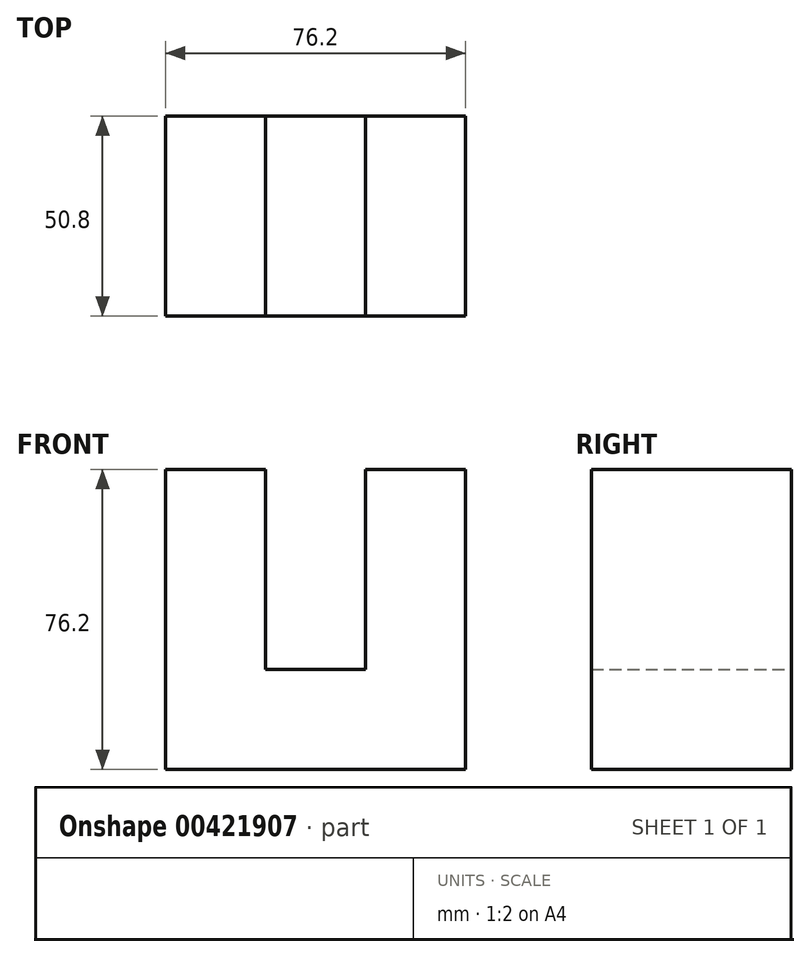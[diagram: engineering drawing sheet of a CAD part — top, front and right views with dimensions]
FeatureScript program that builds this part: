
annotation { "Feature Type Name" : "Feature", "Feature Type Description" : "" }
export const myFeature = defineFeature(function(context is Context, id is Id, definition is map)
    precondition{}
    {
        {
            var Q0;
            Q0=qCreatedBy(makeId("Front.planeOp"),FACE);
            var sketch = newSketch(context, id + "F0", { "sketchPlane" : qUnion([Q0])});
            skLineSegment(sketch, "E0", {"start": v(-51.91, 0) * mm, "end": v(24.29, 0) * mm});
            skLineSegment(sketch, "E1", {"start": v(-51.91, 0) * mm, "end": v(-51.91, 76.2) * mm});
            skLineSegment(sketch, "E2", {"start": v(24.29, 0) * mm, "end": v(24.29, 76.2) * mm});
            skLineSegment(sketch, "E3", {"start": v(-51.91, 76.2) * mm, "end": v(-26.51, 76.2) * mm});
            skLineSegment(sketch, "E4", {"start": v(24.29, 76.2) * mm, "end": v(-1.11, 76.2) * mm});
            skLineSegment(sketch, "E5", {"start": v(-26.51, 76.2) * mm, "end": v(-26.51, 25.4) * mm});
            skLineSegment(sketch, "E6", {"start": v(-1.11, 76.2) * mm, "end": v(-1.11, 25.4) * mm});
            skLineSegment(sketch, "E7", {"start": v(-26.51, 25.4) * mm, "end": v(-1.11, 25.4) * mm});
            skSolve(sketch);
        }
        {
            var Q0;
            Q0=makeQuery(id+"F0.imprint","IMPRINT",FACE,{"disambiguationData":[TD([[makeQuery(id+"F0.imprint","IMPRINT",EDGE,{"derivedFrom":sQuery(id+"F0.wireOp",EDGE,"E0")}),1.0]])]});
            extrude(context, id + "F1", {"entities" : qUnion([Q0]), "depth" : 50.8 * mm});
        }
    });
